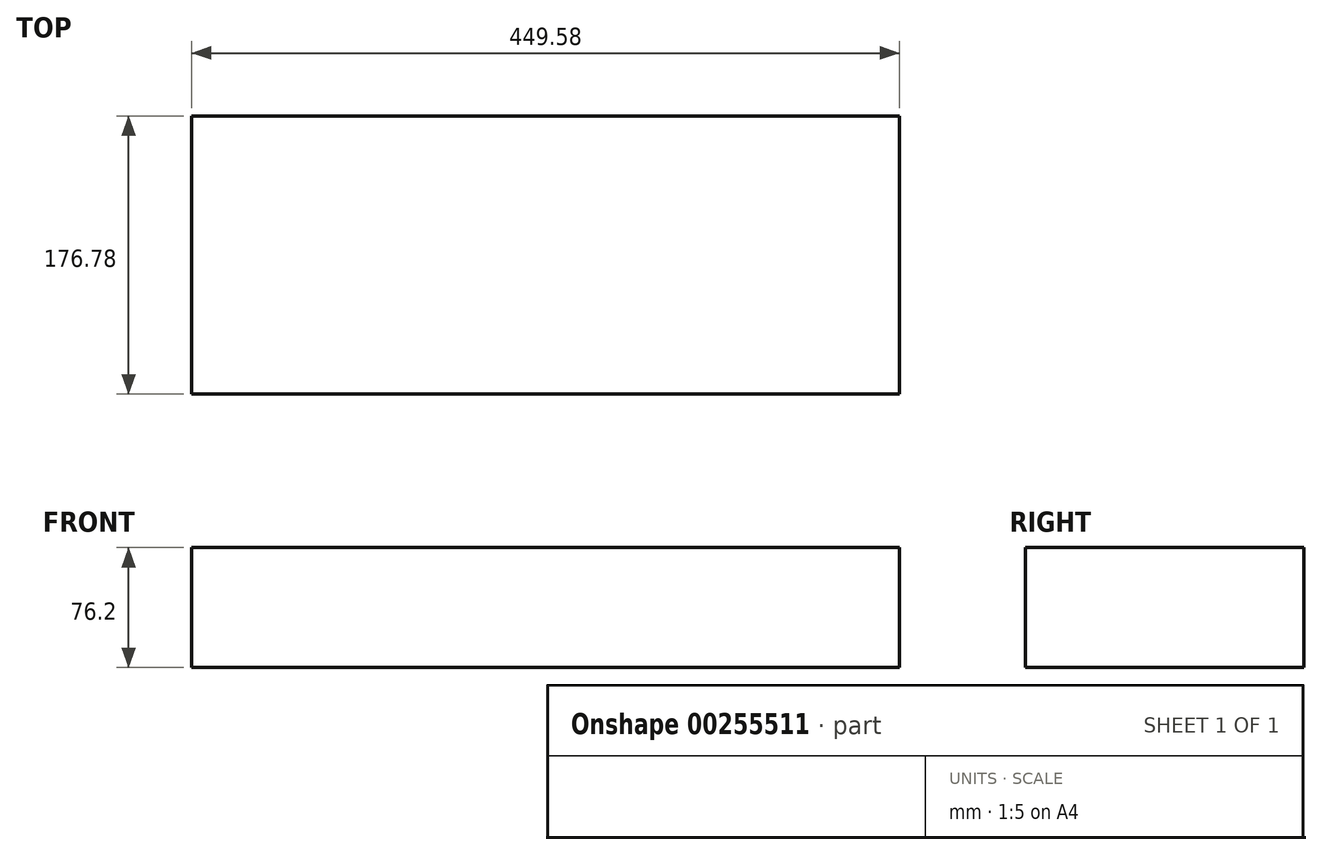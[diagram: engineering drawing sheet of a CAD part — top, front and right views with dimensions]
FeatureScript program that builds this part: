
annotation { "Feature Type Name" : "Feature", "Feature Type Description" : "" }
export const myFeature = defineFeature(function(context is Context, id is Id, definition is map)
    precondition{}
    {
        {
            var Q0;
            Q0=qCreatedBy(makeId("Top.planeOp"),FACE);
            var sketch = newSketch(context, id + "F0", { "sketchPlane" : qUnion([Q0])});
            skLineSegment(sketch, "E0.bottom", {"start": v(-92.09, 134.16) * mm, "end": v(357.5, 134.16) * mm});
            skLineSegment(sketch, "E0.top", {"start": v(-92.09, -42.62) * mm, "end": v(357.5, -42.62) * mm});
            skLineSegment(sketch, "E0.left", {"start": v(-92.09, 134.16) * mm, "end": v(-92.09, -42.62) * mm});
            skLineSegment(sketch, "E0.right", {"start": v(357.5, 134.16) * mm, "end": v(357.5, -42.62) * mm});
            skSolve(sketch);
        }
        {
            var Q0;
            Q0 = qSketchRegion(id + "F0", true);
            extrude(context, id + "F1", {"entities" : qUnion([Q0]), "depth" : 76.2 * mm});
        }
    });
